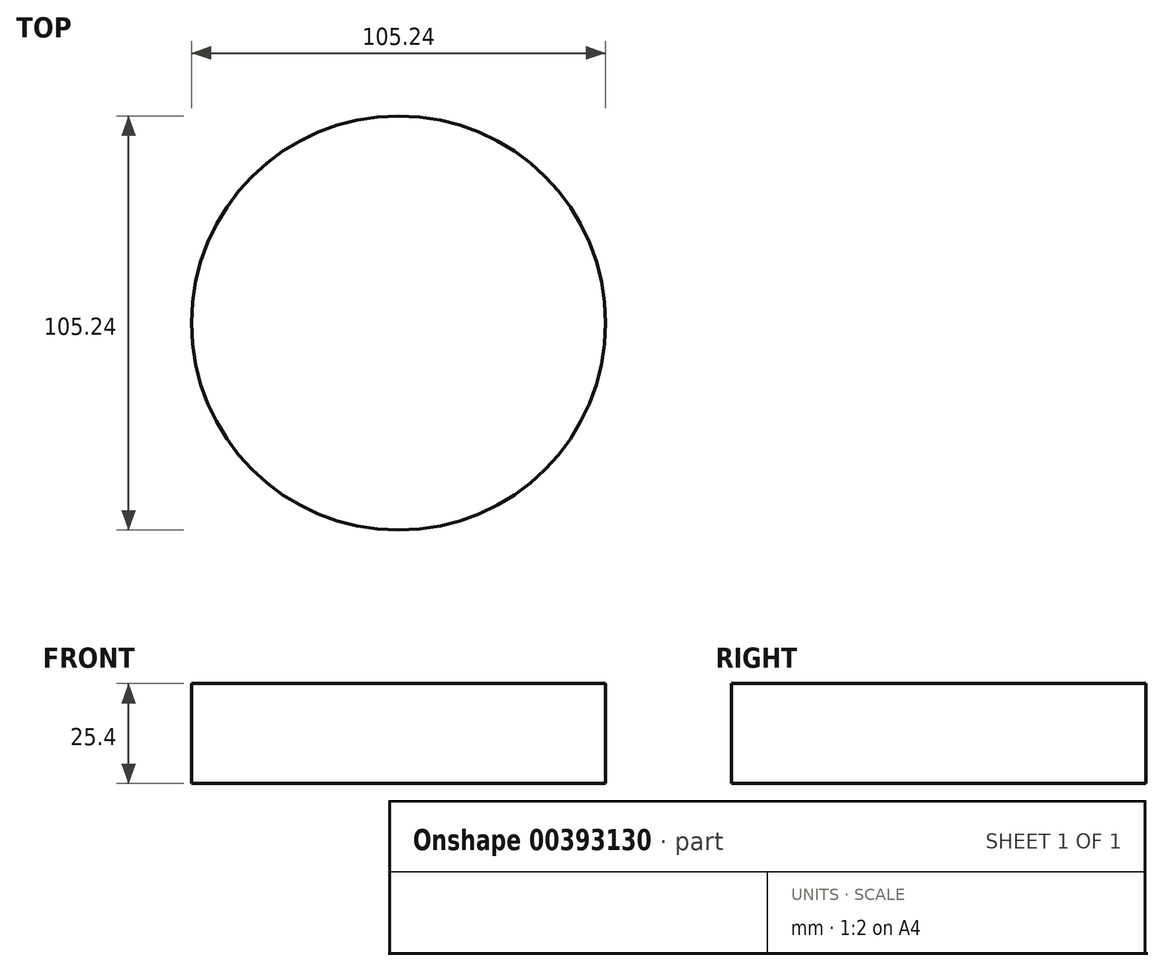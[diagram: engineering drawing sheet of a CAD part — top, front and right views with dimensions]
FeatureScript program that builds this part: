
annotation { "Feature Type Name" : "Feature", "Feature Type Description" : "" }
export const myFeature = defineFeature(function(context is Context, id is Id, definition is map)
    precondition{}
    {
        {
            var Q0;
            Q0=qCreatedBy(makeId("Top.planeOp"),FACE);
            var sketch = newSketch(context, id + "F0", { "sketchPlane" : qUnion([Q0])});
            skCircle(sketch, "E0", {"center": v(0, 0) * mm, "radius": 52.62 * mm});
            skSolve(sketch);
        }
        {
            var Q0;
            Q0 = qSketchRegion(id + "F0", true);
            extrude(context, id + "F1", {"entities" : qUnion([Q0]), "depth" : 25.4 * mm});
        }
    });
